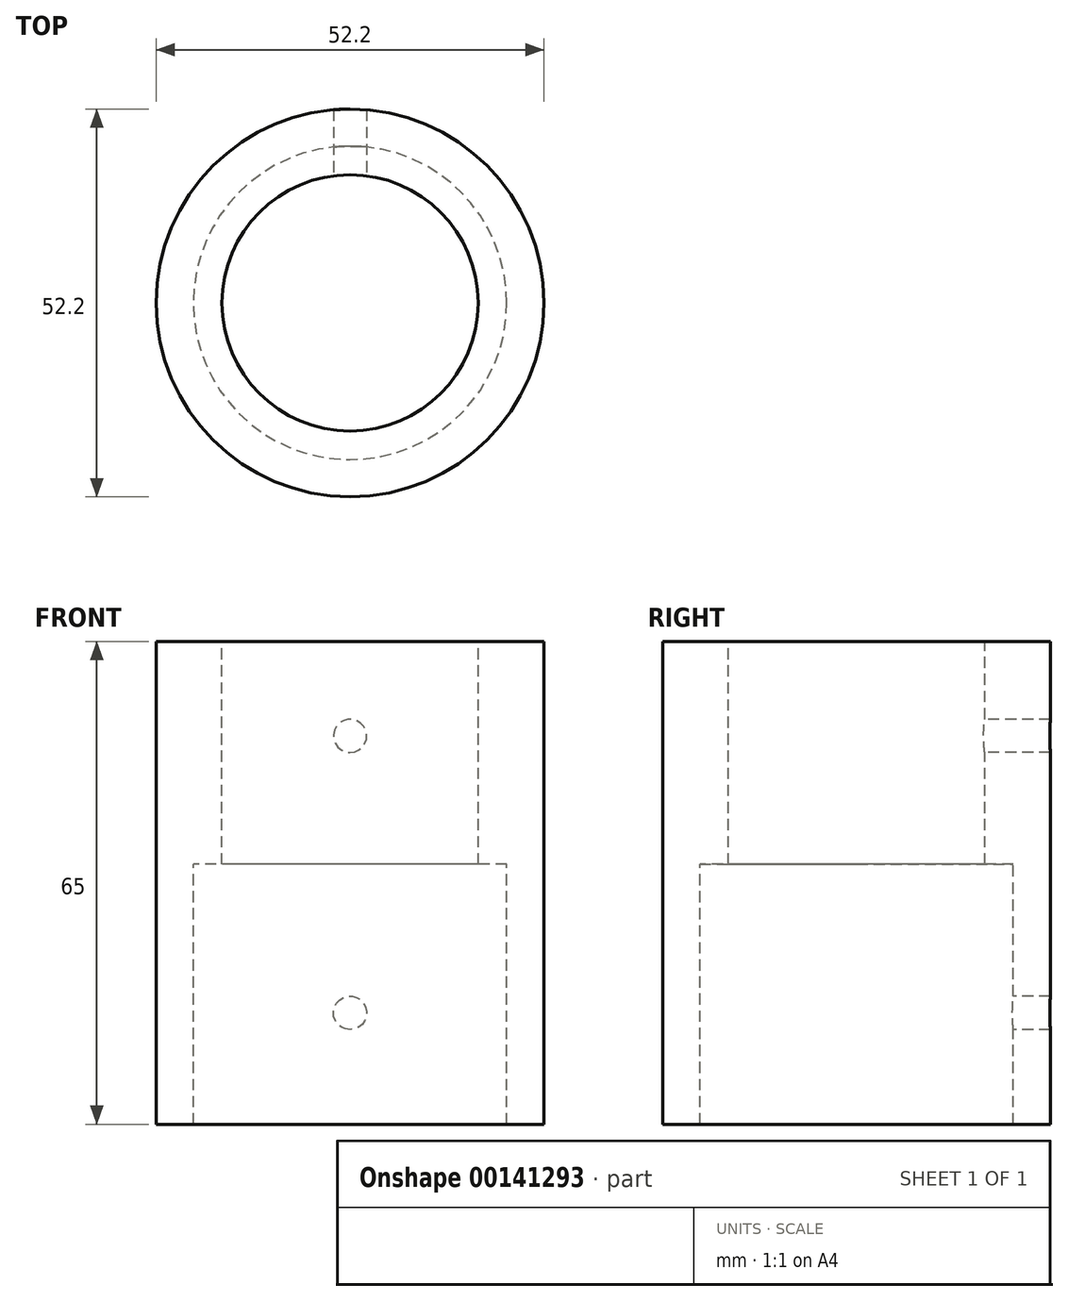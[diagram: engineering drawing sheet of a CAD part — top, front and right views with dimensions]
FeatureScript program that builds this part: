
annotation { "Feature Type Name" : "Feature", "Feature Type Description" : "" }
export const myFeature = defineFeature(function(context is Context, id is Id, definition is map)
    precondition{}
    {
        {
            var Q0;
            Q0=qCreatedBy(makeId("Front.planeOp"),FACE);
            var sketch = newSketch(context, id + "F0", { "sketchPlane" : qUnion([Q0])});
            skLineSegment(sketch, "E0", {"start": v(17.25, 27.5) * mm, "end": v(17.25, 2.5) * mm});
            skLineSegment(sketch, "E1", {"start": v(0, 2.5) * mm, "end": v(0, -2.5) * mm, "construction": true});
            skLineSegment(sketch, "E2", {"start": v(17.25, -2.5) * mm, "end": v(21.1, -2.5) * mm});
            skLineSegment(sketch, "E3", {"start": v(21.1, -2.5) * mm, "end": v(21.1, -37.5) * mm});
            skLineSegment(sketch, "E4", {"start": v(21.1, -37.5) * mm, "end": v(26.1, -37.5) * mm});
            skLineSegment(sketch, "E5", {"start": v(26.1, -37.5) * mm, "end": v(26.1, 27.5) * mm});
            skLineSegment(sketch, "E6", {"start": v(26.1, 27.5) * mm, "end": v(17.25, 27.5) * mm});
            skLineSegment(sketch, "E7", {"start": v(17.25, 2.5) * mm, "end": v(17.25, -2.5) * mm});
            skSolve(sketch);
        }
        {
            var Q0;
            Q0 = qSketchRegion(id + "F0", true);
            var Q1;
            Q1=sQuery(id+"F0.wireOp",EDGE,"E1");
            revolve(context, id + "F1", {"entities" : qUnion([Q0]), "axis" : qUnion([Q1]), "revolveType" : RevolveType.FULL});
        }
        {
            var Q0;
            Q0=qCreatedBy(makeId("Front.planeOp"),FACE);
            var sketch = newSketch(context, id + "F2", { "sketchPlane" : qUnion([Q0])});
            skCircle(sketch, "E8", {"center": v(0, 14.8) * mm, "radius": 2.25 * mm});
            skCircle(sketch, "E9", {"center": v(0, -22.5) * mm, "radius": 2.25 * mm});
            skSolve(sketch);
        }
        {
            var Q0;
            Q0 = qSketchRegion(id + "F2", true);
            extrude(context, id + "F3", {"entities" : qUnion([Q0]), "operationType" : NewBodyOperationType.REMOVE, "oppositeDirection" : true, "depth" : 28 * mm});
        }
    });
